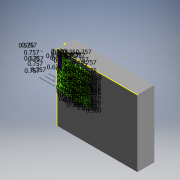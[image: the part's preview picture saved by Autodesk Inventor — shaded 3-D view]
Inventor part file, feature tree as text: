
AUTODESK INVENTOR PART (.ipt)
format: ipt  version: 2018 (Build 220112000, 112)  size: 327,680 bytes
history: native  units: mm (DEFAULTED — no unit token found)
features: extrude x3, sketch x3
ambient origin geometry x8: Origin, YZ Plane, XZ Plane, XY Plane, X Axis, Y Axis, Z Axis, Center Point
bodies: Solid1 (feature_tree)
feature tree (6):
  extrude  "Extrusion1"  Depth=127.254mm
  sketch  "Sketch2"  dims[d2=32.004mm d3=0.0mm d4=5.2578mm]
  extrude  "Extrusion2"  Depth=32.004mm
  extrude  "Extrusion3"  Depth=14.6558mm
  sketch  "Sketch3"  dims[d5=11.6713mm d6=7.5692mm d7=5.26mm d8=7.5692mm d9=5.2578mm d10=7.5692mm d11=7.5692mm d12=5.2578mm d13=7.5692mm d14=7.5692mm d15=7.5692mm d16=7.5692mm d17=7.5692mm d18=7.5692mm d19=7.5692mm d20=7.5692mm d21=7.5692mm d22=7.5692mm d23=3.6576mm d24=14.6558mm d25=0.0mm d26=3.6576mm d27=3.6576mm d28=3.6576mm d29=3.6576mm d30=3.6576mm d31=3.6576mm d32=3.6576mm d33=3.6576mm d34=3.6576mm d35=3.6576mm d36=3.6576mm d37=3.6576mm d38=3.6576mm d39=3.6576mm d40=3.6576mm d41=3.6576mm d42=3.6576mm d43=3.6576mm d44=3.6576mm d45=3.6576mm d46=3.6576mm d47=3.6576mm d48=3.6576mm d49=3.6576mm d50=3.6576mm d51=3.6576mm d52=3.6576mm d53=3.6576mm d54=3.6576mm d55=3.6576mm d56=3.6576mm d57=3.6576mm d58=3.6576mm d59=3.6576mm d60=3.6576mm d61=3.6576mm d62=3.6576mm d63=3.6576mm d64=3.6576mm d65=3.6576mm d66=3.6576mm d67=3.6576mm d68=3.6576mm d69=3.6576mm d70=3.6576mm d71=3.6576mm d72=3.6576mm d73=3.6576mm d74=3.6576mm d75=3.6576mm d76=3.6576mm d77=3.6576mm d78=3.6576mm d79=3.6576mm d80=3.6576mm d81=3.6576mm d82=3.6576mm d83=3.6576mm d84=3.6576mm d85=3.6576mm d86=3.6576mm d87=3.6576mm d88=3.6576mm d89=3.6576mm d90=14.6558mm d91=0.0mm d92=6.35mm d93=6.35mm d94=6.35mm d95=6.35mm d96=6.35mm d97=6.35mm d98=6.35mm d99=6.35mm d100=6.35mm d101=6.35mm d102=6.35mm d103=6.35mm d104=6.35mm d105=6.35mm d106=6.35mm d107=6.35mm d108=6.35mm d109=6.35mm d110=6.35mm d111=6.35mm d112=6.35mm d113=6.35mm d114=6.35mm d115=6.35mm d116=6.35mm d117=6.35mm d118=6.35mm d119=6.35mm d120=6.35mm d121=6.35mm d122=6.35mm d123=6.35mm d124=6.35mm d125=6.35mm d126=6.35mm d127=6.35mm d128=6.35mm d129=6.35mm d130=6.35mm d131=6.35mm d132=6.35mm d133=6.35mm d134=6.35mm d135=6.35mm d136=6.35mm d137=6.35mm d138=6.35mm d139=6.35mm d140=6.35mm d141=6.35mm d142=6.35mm d143=6.35mm d144=6.35mm d145=6.35mm d146=6.35mm d147=6.35mm d148=6.35mm d149=6.35mm d150=6.35mm d151=6.35mm d152=6.35mm d153=6.35mm d154=6.35mm d155=6.35mm d156=6.35mm]
  sketch  "Sketch1"  dims[d0=153.162mm d1=127.254mm]
